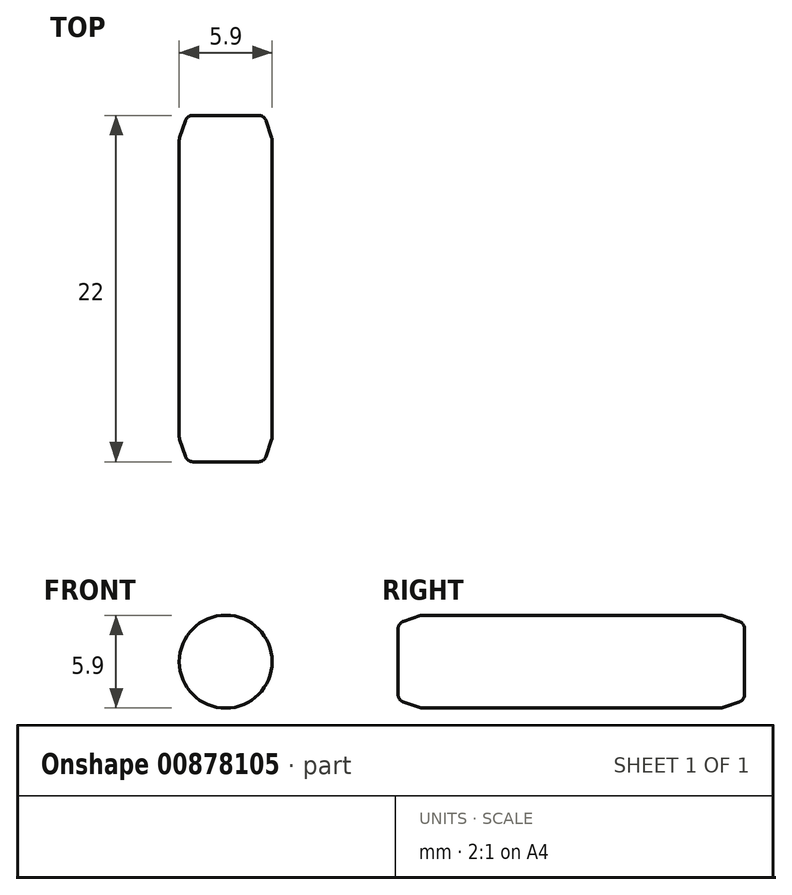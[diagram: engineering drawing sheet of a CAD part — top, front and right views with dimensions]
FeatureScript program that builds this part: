
annotation { "Feature Type Name" : "Feature", "Feature Type Description" : "" }
export const myFeature = defineFeature(function(context is Context, id is Id, definition is map)
    precondition{}
    {
        {
            var Q0;
            Q0=qCreatedBy(makeId("Front.planeOp"),FACE);
            var sketch = newSketch(context, id + "F0", { "sketchPlane" : qUnion([Q0])});
            skCircle(sketch, "E0", {"center": v(0, 0) * mm, "radius": 2.95 * mm});
            skSolve(sketch);
        }
        {
            var Q0;
            Q0 = qSketchRegion(id + "F0", true);
            extrude(context, id + "F1", {"entities" : qUnion([Q0]), "oppositeDirection" : true, "depth" : 22 * mm, "offsetDistance" : 25 * mm});
        }
        {
            var Q0;
            Q0=makeQuery(id+"F1.opExtrude","CAP_EDGE",EDGE,{"disambiguationData":[OSD([sQuery(id+"F0.wireOp",EDGE,"E0")])],"isStart":true});
            var Q1;
            Q1=makeQuery(id+"F1.opExtrude","CAP_EDGE",EDGE,{"disambiguationData":[OSD([sQuery(id+"F0.wireOp",EDGE,"E0")])],"isStart":false});
            chamfer(context, id + "F2", {"entities" : qUnion([Q0, Q1]), "chamferType" : ChamferType.TWO_OFFSETS, "width1" : .5 * mm, "oppositeDirection" : false, "width2" : 1.5 * mm, "tangentPropagation" : true});
        }
        {
            var Q0;
            {var subQ0=sQuery(id+"F0.wireOp",EDGE,"E0");Q0=makeQuery(id+"F2.opChamfer","BLEND_EDGE",EDGE,{"blendedFrom":[makeQuery(id+"F1.opExtrude","CAP_EDGE",EDGE,{"disambiguationData":[OSD([subQ0])],"isStart":true}),makeQuery(id+"F1.opExtrude","CAP_FACE",FACE,{"disambiguationData":[OSD([subQ0])],"isStart":true})],"blendedInto":[makeQuery(id+"F1.opExtrude","CAP_FACE",FACE,{"disambiguationData":[OSD([subQ0])],"isStart":true})]});}
            var Q1;
            {var subQ0=sQuery(id+"F0.wireOp",EDGE,"E0");Q1=makeQuery(id+"F2.opChamfer","BLEND_EDGE",EDGE,{"blendedFrom":[makeQuery(id+"F1.opExtrude","CAP_EDGE",EDGE,{"disambiguationData":[OSD([subQ0])],"isStart":false}),makeQuery(id+"F1.opExtrude","CAP_FACE",FACE,{"disambiguationData":[OSD([subQ0])],"isStart":false})],"blendedInto":[makeQuery(id+"F1.opExtrude","CAP_FACE",FACE,{"disambiguationData":[OSD([subQ0])],"isStart":false})]});}
            var Q2;
            {var subQ0=sQuery(id+"F0.wireOp",EDGE,"E0");Q2=makeQuery(id+"F2.opChamfer","BLEND_EDGE",EDGE,{"blendedFrom":[makeQuery(id+"F1.opExtrude","CAP_EDGE",EDGE,{"disambiguationData":[OSD([subQ0])],"isStart":true}),makeQuery(id+"F1.opExtrude","SWEPT_FACE",FACE,{"disambiguationData":[OSD([subQ0])]})],"blendedInto":[makeQuery(id+"F1.opExtrude","SWEPT_FACE",FACE,{"disambiguationData":[OSD([subQ0])]})]});}
            var Q3;
            {var subQ0=sQuery(id+"F0.wireOp",EDGE,"E0");Q3=makeQuery(id+"F2.opChamfer","BLEND_EDGE",EDGE,{"blendedFrom":[makeQuery(id+"F1.opExtrude","CAP_EDGE",EDGE,{"disambiguationData":[OSD([subQ0])],"isStart":false}),makeQuery(id+"F1.opExtrude","SWEPT_FACE",FACE,{"disambiguationData":[OSD([subQ0])]})],"blendedInto":[makeQuery(id+"F1.opExtrude","SWEPT_FACE",FACE,{"disambiguationData":[OSD([subQ0])]})]});}
            fillet(context, id + "F3", {"entities" : qUnion([Q0, Q1, Q2, Q3]), "radius" : .5 * mm, "tangentPropagation" : true, "allowEdgeOverflow" : false});
        }
    });
